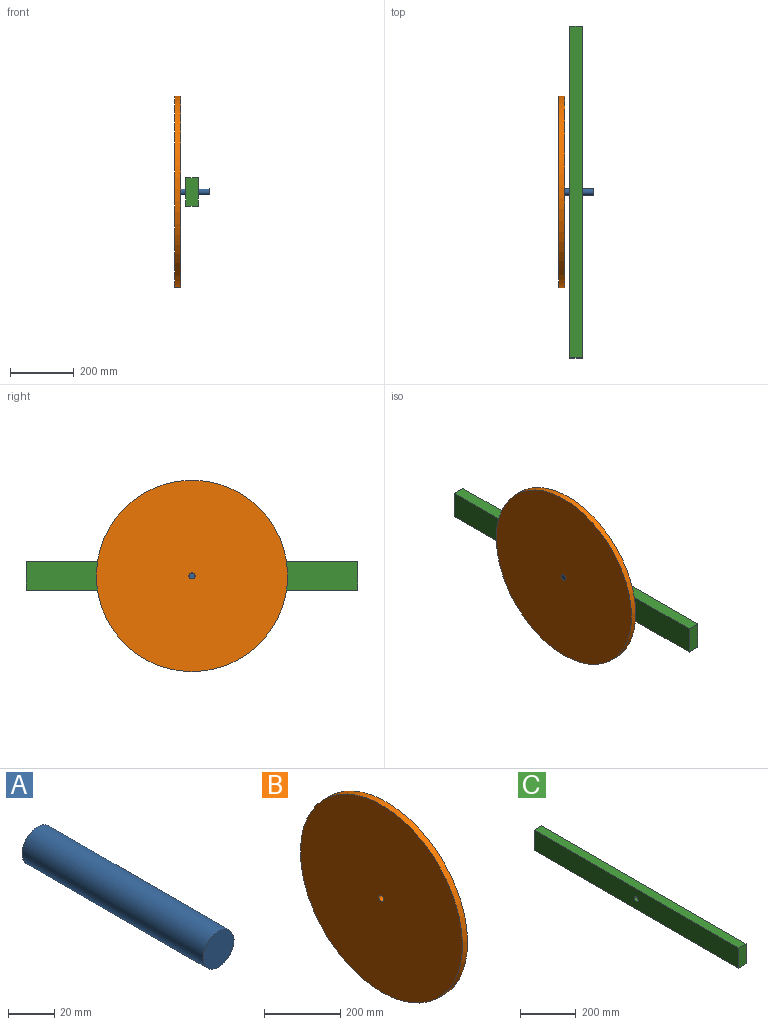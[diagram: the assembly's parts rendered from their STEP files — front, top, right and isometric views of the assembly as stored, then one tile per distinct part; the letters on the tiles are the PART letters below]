
ASSEMBLY  parts=3 mates=2
PART A: 3 faces, bbox 19.1x111.1x19.1 mm
  f0: cylinder r=9.53mm len=111.13mm, axis (0,1,0), area 6650.5mm2, adj f1,f2
  f1: plane 19.05x19.05mm, normal (0,-1,0), area 285mm2, adj f0
  f2: plane 19.05x19.05mm, normal (0,1,0), area 285mm2, adj f0
PART B: 4 faces, bbox 19.1x600x600 mm
  f0: cylinder r=9.53mm len=19.05mm, axis (-1,0,0), area 1140.1mm2, adj f2,f3
  f1: cylinder r=300mm len=600mm, axis (-1,0,0), area 35908.3mm2, adj f2,f3
  f2: plane 600x600mm, normal (1,0,0), area 282457.2mm2, adj f0,f1
  f3: plane 600x600mm, normal (-1,0,0), area 282457.2mm2, adj f0,f1
PART C: 7 faces, bbox 38.1x1041.4x88.9 mm
  f0: plane 88.9x38.1mm, normal (0,-1,0), area 3387.1mm2, adj f1,f3,f4,f5
  f1: plane 1041.4x38.1mm, normal (0,0,-1), area 39677.3mm2, adj f0,f2,f4,f5
  f2: plane 88.9x38.1mm, normal (0,1,0), area 3387.1mm2, adj f1,f3,f4,f5
  f3: plane 1041.4x38.1mm, normal (0,0,1), area 39677.3mm2, adj f0,f2,f4,f5
  f4: plane 1041.4x88.9mm, normal (1,0,0), area 92295.4mm2, adj f0,f1,f2,f3,f6
  f5: plane 1041.4x88.9mm, normal (-1,0,0), area 92295.4mm2, adj f0,f1,f2,f3,f6
  f6: cylinder r=9.53mm len=38.1mm, axis (1,0,0), area 2280.2mm2, adj f4,f5
PLACE A rot(axis=(0,0,-1),90deg) t=(-165.54,232.58,206.53)mm
PLACE B t=(-275.07,232.58,206.53)mm
PLACE C t=(-240.15,-216.81,173.65)mm
MATE fastened B.f1 <-> A.f0  axis (-1,0,0) through (-275.07,232.58,206.53)mm
MATE fastened A.f0 <-> C.f6  axis (-1,0,0) through (-276.66,232.58,206.53)mm
